# Revit family: FallProtection_RopeAccessNeedle_Kattsafe_1200AFrame
name_source: partatom
category: Specialty Equipment
units: mm (PartAtom-declared; Revit-internal decimal feet)

## family parameters
Always vertical = Yes
Cut with Voids When Loaded = No
Enable Cutting in Views = No
Maintain Annotation Orientation = No
OmniClass Number = 23.27.71.21
Part Type = Normal
Room Calculation Point = No
Round Connector Dimension = Use Diameter
Shared = No
Work Plane-Based = No

## types (15) — shared parameters
Assembly Code = E1090100
BracePinHeight = 512 mm  [stored 1.67979 ft]
Description = Kattsafe needles are designed for rope access on roofs where the load needs to be spread to avoid damaging the roof area, and for roofs with no parapets.
ElementType = Fall Protection
Export Type to IFC As = IfcBuildingElementProxyType
FramePinHeight = 1206 mm
IfcExportAs = IfcBuildingElementProxyType
IfcExportType = USERDEFINED
Manufacturer = Kattsafe®
ManufacturerOverallWidth = 1817 mm  [stored 5.96129 ft]
ManufacturerURLProductSpecific = https://kattsafe.com.au
Material = Aluminum_Kattsafe_Satin
ModifiedIssue = 20240430 $
RearAttachmentType = Rearattachment_Kattsafe_Needle : Horizontal Trolley (OH448A)
Type IFC Predefined Type = USERDEFINED
URL = https://kattsafe.com.au
Uniclass2015Code = Pr_40_70_75_21
Uniclass2015Title = Davit arms
Uniclass2015Version = Products v1.23
zero-valued in all types: Default Elevation

## per-type parameters (varying)
| type | 1200Extension | 1500Extension | 1800Extension | BraceLength | CantileverSizeSelector | ExtendableBoom | ExtendedBraceLengthCalc | MainBoomCenterExtension | ManufacturerSpecCode | Model | RearBeamAngledHeightCalc | RearBeamHeight | RearBeamWidth | RearFixingHeight | RearMemberFixingPointCalc | TrolleyAlignOffset | Type Comments |
| 1200 Cantilever - Horizontal Trolley (OH412.1200 + OH448A) | Yes | No | No | 1000 mm  [stored 3.28084 ft] | 1 | No | 950 mm  [stored 3.1168 ft] | 0 mm  [stored 0 ft] | OH412.12 + OH448A | OH412.12 + OH448A | 160 mm  [stored 0.524934 ft] | 180 mm  [stored 0.590551 ft] | 60 mm  [stored 0.19685 ft] | 42 mm  [stored 0.137795 ft] | 70 mm  [stored 0.229659 ft] | 15 mm  [stored 0.0492126 ft] | 1200mm A-Frame - 1200mm Extension - Horizontal Trolley Rear Attachment |
| 1200 Cantilever - Vertical Trolley (OH412.1200 + OH449A) | Yes | No | No | 1000 mm  [stored 3.28084 ft] | 1 | No | 950 mm  [stored 3.1168 ft] | 0 mm  [stored 0 ft] | OH412.12 + OH449A | OH412.12 + OH449A | 160 mm  [stored 0.524934 ft] | 180 mm  [stored 0.590551 ft] | 60 mm  [stored 0.19685 ft] | 67 mm | 70 mm  [stored 0.229659 ft] | 33 mm  [stored 0.108268 ft] | 1200mm A-Frame - 1200mm Extension - Vertical Trolley Rear Attachment |
| 1200 Cantilever - Wide Deck Mount (OH412.1200 + OH444W) | Yes | No | No | 1000 mm  [stored 3.28084 ft] | 1 | No | 950 mm  [stored 3.1168 ft] | 0 mm  [stored 0 ft] | OH412.12 + OH444W | OH412.12 + OH444W | 160 mm  [stored 0.524934 ft] | 180 mm  [stored 0.590551 ft] | 60 mm  [stored 0.19685 ft] | 125 mm  [stored 0.410105 ft] | 70 mm  [stored 0.229659 ft] | 0 mm  [stored 0 ft] | 1200mm A-Frame - 1200mm Extension - Wide Deck Mount Rear Attachment |
| 1200 Cantilever - Metal Deck Mount (OH412.1200 + OH444A) | Yes | No | No | 1000 mm  [stored 3.28084 ft] | 1 | No | 950 mm  [stored 3.1168 ft] | 0 mm  [stored 0 ft] | OH412.12 + OH444A | OH412.12 + OH444A | 160 mm  [stored 0.524934 ft] | 180 mm  [stored 0.590551 ft] | 60 mm  [stored 0.19685 ft] | 123 mm  [stored 0.403543 ft] | 70 mm  [stored 0.229659 ft] | 0 mm  [stored 0 ft] | 1200mm A-Frame - 1200mm Extension - Metal Deck Mount Rear Attachment |
| 1800 Cantilever - Horizontal Trolley (OH412.1800 + OH448A) | No | No | Yes | 1500 mm  [stored 4.92126 ft] | 3 | Yes | 1450 mm  [stored 4.75722 ft] | 1225 mm  [stored 4.01903 ft] | OH412.18 + OH448A | OH412.18 + OH448A | 170 mm | 190 mm  [stored 0.62336 ft] | 70 mm  [stored 0.229659 ft] | 42 mm  [stored 0.137795 ft] | 75 mm | 15 mm  [stored 0.0492126 ft] | 1200mm A-Frame - 1800mm Extension - Horizontal Trolley Rear Attachment |
| 1800 Cantilever - Vertical Trolley (OH412.1800 + OH449A) | No | No | Yes | 1500 mm  [stored 4.92126 ft] | 3 | Yes | 1450 mm  [stored 4.75722 ft] | 1225 mm  [stored 4.01903 ft] | OH412.18 + OH449A | OH412.18 + OH449A | 170 mm | 190 mm  [stored 0.62336 ft] | 70 mm  [stored 0.229659 ft] | 67 mm | 75 mm | 33 mm  [stored 0.108268 ft] | 1200mm A-Frame - 1800mm Extension - Vertical Trolley Rear Attachment |
| 1800 Cantilever - Wide Deck Mount (OH412.1800 + OH444W) | No | No | Yes | 1500 mm  [stored 4.92126 ft] | 3 | Yes | 1450 mm  [stored 4.75722 ft] | 1225 mm  [stored 4.01903 ft] | OH412.18 + OH444W | OH412.18 + OH444W | 170 mm | 190 mm  [stored 0.62336 ft] | 70 mm  [stored 0.229659 ft] | 125 mm  [stored 0.410105 ft] | 75 mm | 0 mm  [stored 0 ft] | 1200mm A-Frame - 1800mm Extension - Wide Deck Mount Rear Attachment |
| 1800 Cantilever - Metal Deck Mount (OH412.1800 + OH444A) | No | No | Yes | 1500 mm  [stored 4.92126 ft] | 3 | Yes | 1450 mm  [stored 4.75722 ft] | 1225 mm  [stored 4.01903 ft] | OH412.18 + OH444A | OH412.18 + OH444A | 170 mm | 190 mm  [stored 0.62336 ft] | 70 mm  [stored 0.229659 ft] | 123 mm  [stored 0.403543 ft] | 75 mm | 0 mm  [stored 0 ft] | 1200mm A-Frame - 1800mm Extension - Metal Deck Mount Rear Attachment |
| 1800 Cantilever - Concrete Mount (OH412.1800 + OH443) | No | No | Yes | 1500 mm  [stored 4.92126 ft] | 3 | Yes | 1450 mm  [stored 4.75722 ft] | 1225 mm  [stored 4.01903 ft] | OH412.18 + OH443 | OH412.18 + OH443 | 170 mm | 190 mm  [stored 0.62336 ft] | 70 mm  [stored 0.229659 ft] | 119 mm  [stored 0.39042 ft] | 75 mm | 0 mm  [stored 0 ft] | 1200mm A-Frame - 1800mm Extension - Concrete Mount Rear Attachment |
| 1500 Cantilever - Horizontal Trolley (OH412.1500 + OH448A) | No | Yes | No | 1200 mm | 2 | Yes | 1150 mm | 1045 mm  [stored 3.42848 ft] | OH412.15 + OH448A | OH412.15 + OH448A | 170 mm | 190 mm  [stored 0.62336 ft] | 70 mm  [stored 0.229659 ft] | 42 mm  [stored 0.137795 ft] | 75 mm | 15 mm  [stored 0.0492126 ft] | 1200mm A-Frame - 1500mm Extension - Horizontal Trolley Rear Attachment |
| 1500 Cantilever - Vertical Trolley (OH412.1500 + OH449A) | No | Yes | No | 1200 mm | 2 | Yes | 1150 mm | 1045 mm  [stored 3.42848 ft] | OH412.15 + OH449A | OH412.15 + OH449A | 170 mm | 190 mm  [stored 0.62336 ft] | 70 mm  [stored 0.229659 ft] | 67 mm | 75 mm | 33 mm  [stored 0.108268 ft] | 1200mm A-Frame - 1500mm Extension - Vertical Trolley Rear Attachment |
| 1500 Cantilever - Wide Deck Mount (OH412.1500 + OH444W) | No | Yes | No | 1200 mm | 2 | Yes | 1150 mm | 1045 mm  [stored 3.42848 ft] | OH412.15 + OH444W | OH412.15 + OH444W | 170 mm | 190 mm  [stored 0.62336 ft] | 70 mm  [stored 0.229659 ft] | 125 mm  [stored 0.410105 ft] | 75 mm | 0 mm  [stored 0 ft] | 1200mm A-Frame - 1500mm Extension - Wide Deck Mount Rear Attachment |
| 1500 Cantilever - Metal Deck Mount (OH412.1500 + OH444A) | No | Yes | No | 1200 mm | 2 | Yes | 1150 mm | 1045 mm  [stored 3.42848 ft] | OH412.15 + OH444A | OH412.15 + OH444A | 170 mm | 190 mm  [stored 0.62336 ft] | 70 mm  [stored 0.229659 ft] | 123 mm  [stored 0.403543 ft] | 75 mm | 0 mm  [stored 0 ft] | 1200mm A-Frame - 1500mm Extension - Metal Deck Mount Rear Attachment |
| 1500 Cantilever - Concrete Mount (OH412.1500 + OH443) | No | Yes | No | 1200 mm | 2 | Yes | 1150 mm | 1045 mm  [stored 3.42848 ft] | OH412.15 + OH443 | OH412.15 + OH443 | 170 mm | 190 mm  [stored 0.62336 ft] | 70 mm  [stored 0.229659 ft] | 119 mm  [stored 0.39042 ft] | 75 mm | 0 mm  [stored 0 ft] | 1200mm A-Frame - 1500mm Extension - Concrete Mount Rear Attachment |
| 1200 Cantilever - Concrete Mount (OH412.1200 + OH443) | Yes | No | No | 1000 mm  [stored 3.28084 ft] | 1 | No | 950 mm  [stored 3.1168 ft] | 0 mm  [stored 0 ft] | OH412.12 + OH443 | OH412.12 + OH443 | 160 mm  [stored 0.524934 ft] | 180 mm  [stored 0.590551 ft] | 60 mm  [stored 0.19685 ft] | 119 mm  [stored 0.39042 ft] | 70 mm  [stored 0.229659 ft] | 0 mm  [stored 0 ft] | 1200mm A-Frame - 1200mm Extension - Concrete Mount Rear Attachment |

note: [stored X ft] marks values corroborated as IEEE doubles in the binary element streams (Revit-internal decimal feet)

## geometry (parser evidence)
native form markers: Sweep x8
no freeform markers — native parametric forms only
